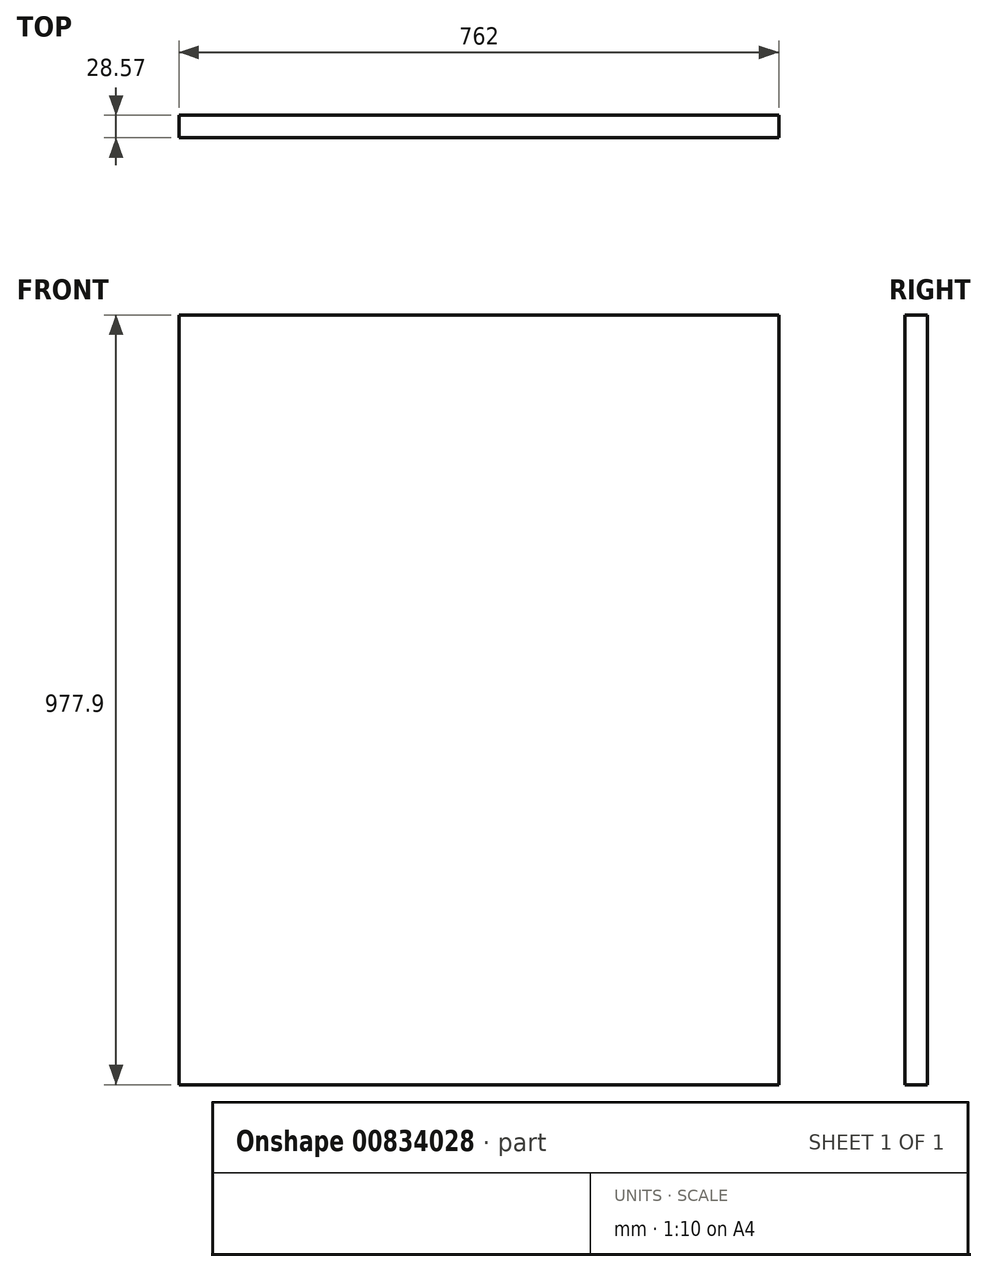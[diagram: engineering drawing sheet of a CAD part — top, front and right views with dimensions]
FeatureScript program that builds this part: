
annotation { "Feature Type Name" : "Feature", "Feature Type Description" : "" }
export const myFeature = defineFeature(function(context is Context, id is Id, definition is map)
    precondition{}
    {
        {
            var Q0;
            Q0=qCreatedBy(makeId("Front.planeOp"),FACE);
            var sketch = newSketch(context, id + "F0", { "sketchPlane" : qUnion([Q0])});
            skLineSegment(sketch, "E0.bottom", {"start": v(381, 488.95) * mm, "end": v(-381, 488.95) * mm});
            skLineSegment(sketch, "E0.top", {"start": v(381, -488.95) * mm, "end": v(-381, -488.95) * mm});
            skLineSegment(sketch, "E0.left", {"start": v(381, 488.95) * mm, "end": v(381, -488.95) * mm});
            skLineSegment(sketch, "E0.right", {"start": v(-381, 488.95) * mm, "end": v(-381, -488.95) * mm});
            skPoint(sketch, "E0.middle", {"position": v(0, 0) * mm});
            skSolve(sketch);
        }
        {
            var Q0;
            Q0=makeQuery(id+"F0.imprint","IMPRINT",FACE,{"disambiguationData":[TD([[makeQuery(id+"F0.imprint","IMPRINT",EDGE,{"derivedFrom":sQuery(id+"F0.wireOp",EDGE,"E0.bottom")}),1.0]])]});
            extrude(context, id + "F1", {"entities" : qUnion([Q0]), "depth" : 28.57 * mm, "offsetDistance" : 25.4 * mm});
        }
    });
